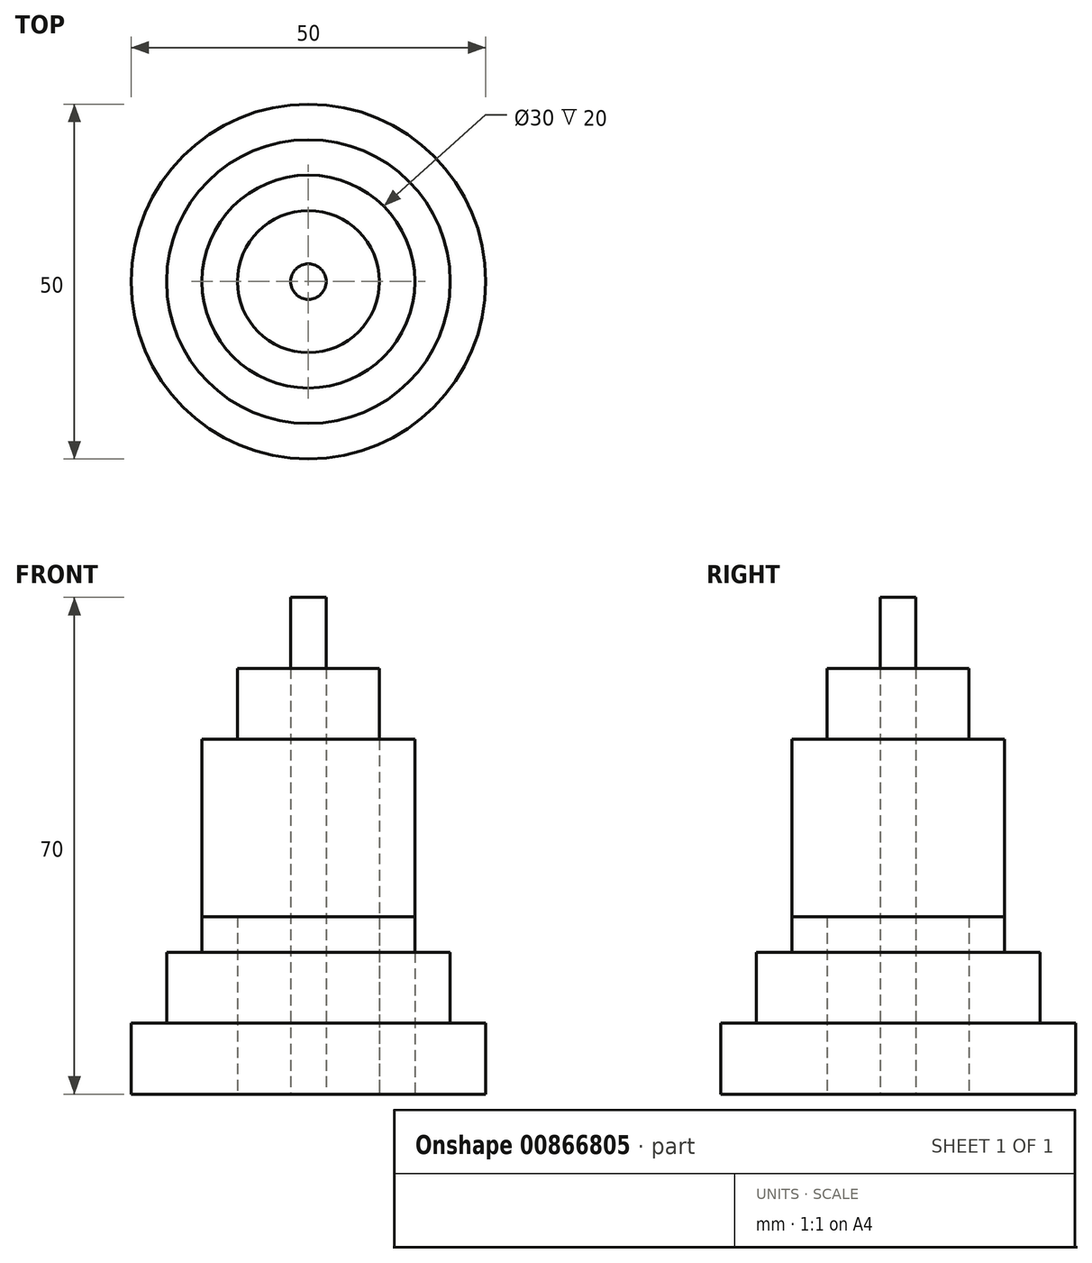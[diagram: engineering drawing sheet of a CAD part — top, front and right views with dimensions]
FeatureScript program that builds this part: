
annotation { "Feature Type Name" : "Feature", "Feature Type Description" : "" }
export const myFeature = defineFeature(function(context is Context, id is Id, definition is map)
    precondition{}
    {
        {
            var Q0;
            Q0=qCreatedBy(makeId("Top.planeOp"),FACE);
            var sketch = newSketch(context, id + "F0", { "sketchPlane" : qUnion([Q0])});
            skCircle(sketch, "E0", {"center": v(0, 0) * mm, "radius": 25 * mm});
            skCircle(sketch, "E1", {"center": v(0, 0) * mm, "radius": 20 * mm});
            skCircle(sketch, "E2", {"center": v(0, 0) * mm, "radius": 15 * mm});
            skCircle(sketch, "E3", {"center": v(0, 0) * mm, "radius": 2.5 * mm});
            skCircle(sketch, "E4", {"center": v(0, 0) * mm, "radius": 10 * mm});
            skSolve(sketch);
        }
        {
            var Q0;
            Q0=makeQuery(id+"F0.imprint","IMPRINT",FACE,{"disambiguationData":[TD([[makeQuery(id+"F0.imprint","IMPRINT",EDGE,{"derivedFrom":sQuery(id+"F0.wireOp",EDGE,"E3")}),1.0]])]});
            extrude(context, id + "F1", {"entities" : qUnion([Q0]), "depth" : 70 * mm, "offsetDistance" : 25 * mm});
        }
        {
            var Q0;
            Q0=makeQuery(id+"F0.imprint","IMPRINT",FACE,{"disambiguationData":[TD([[makeQuery(id+"F0.imprint","IMPRINT",EDGE,{"derivedFrom":sQuery(id+"F0.wireOp",EDGE,"E0")}),1.0]])]});
            extrude(context, id + "F2", {"entities" : qUnion([Q0]), "depth" : 10 * mm, "offsetDistance" : 25 * mm});
        }
        {
            var Q0;
            Q0=makeQuery(id+"F0.imprint","IMPRINT",FACE,{"disambiguationData":[TD([[makeQuery(id+"F0.imprint","IMPRINT",EDGE,{"derivedFrom":sQuery(id+"F0.wireOp",EDGE,"E1")}),1.0]])]});
            extrude(context, id + "F3", {"entities" : qUnion([Q0]), "operationType" : NewBodyOperationType.ADD, "depth" : 20 * mm, "offsetDistance" : 25 * mm});
        }
        {
            var Q0;
            Q0=makeQuery(id+"F0.imprint","IMPRINT",FACE,{"disambiguationData":[TD([[makeQuery(id+"F0.imprint","IMPRINT",EDGE,{"derivedFrom":sQuery(id+"F0.wireOp",EDGE,"E2")}),1.0]])]});
            extrude(context, id + "F4", {"entities" : qUnion([Q0]), "depth" : 25 * mm, "offsetDistance" : 25 * mm});
        }
        {
            var Q0;
            Q0=makeQuery(id+"F4.opExtrude","CAP_FACE",FACE,{"disambiguationData":[OSD([sQuery(id+"F0.wireOp",EDGE,"E2"),sQuery(id+"F0.wireOp",EDGE,"E3")])],"isStart":false});
            cPlane(context, id + "F5", {"entities" : qUnion([Q0]), "cplaneType" : CPlaneType.OFFSET, "offset" : 0 * mm, "width" : 150 * mm, "height" : 150 * mm});
        }
        {
            var Q0;
            Q0=qCreatedBy(id+"F5.planeOp",FACE);
            var sketch = newSketch(context, id + "F6", { "sketchPlane" : qUnion([Q0])});
            skCircle(sketch, "E5", {"center": v(0, 0) * mm, "radius": 15 * mm});
            skSolve(sketch);
        }
        {
            var Q0;
            Q0=makeQuery(id+"F6.imprint","IMPRINT",FACE,{"disambiguationData":[TD([[makeQuery(id+"F6.imprint","IMPRINT",EDGE,{"derivedFrom":sQuery(id+"F6.wireOp",EDGE,"E5")}),1.0]])]});
            extrude(context, id + "F7", {"entities" : qUnion([Q0]), "depth" : 25 * mm, "offsetDistance" : 25 * mm});
        }
        {
            var Q0;
            Q0=makeQuery(id+"F0.imprint","IMPRINT",FACE,{"disambiguationData":[TD([[makeQuery(id+"F0.imprint","IMPRINT",EDGE,{"derivedFrom":sQuery(id+"F0.wireOp",EDGE,"E3")}),-1.0]])]});
            extrude(context, id + "F8", {"entities" : qUnion([Q0]), "depth" : 60 * mm, "offsetDistance" : 25 * mm});
        }
    });
